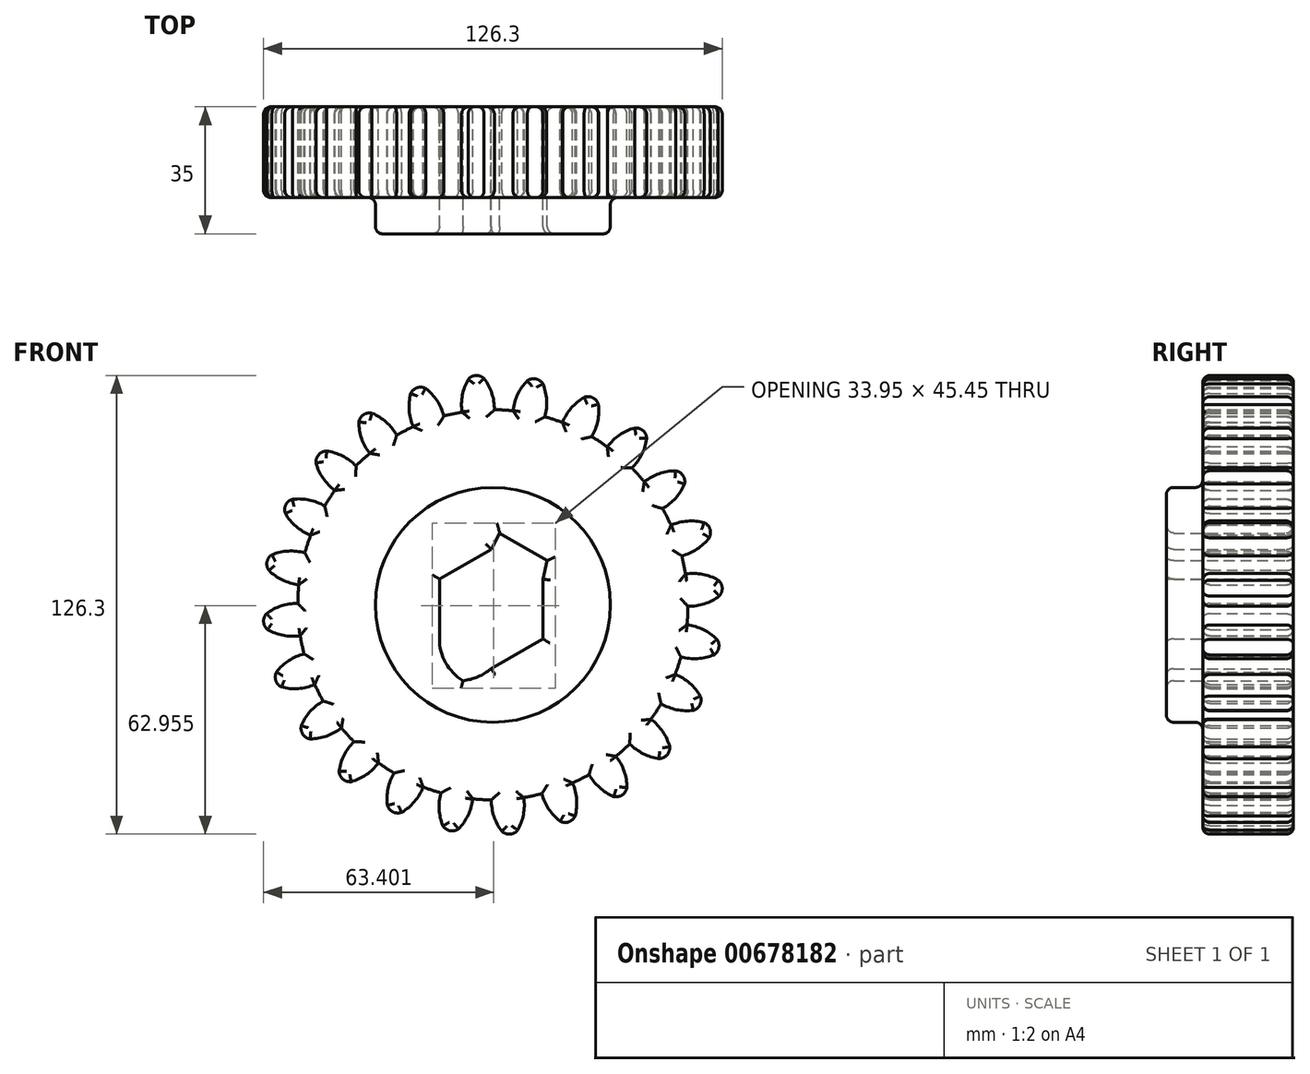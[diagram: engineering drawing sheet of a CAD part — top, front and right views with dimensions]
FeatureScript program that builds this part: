
annotation { "Feature Type Name" : "Feature", "Feature Type Description" : "" }
export const myFeature = defineFeature(function(context is Context, id is Id, definition is map)
    precondition{}
    {
        {
            var Q0;
            Q0=qCreatedBy(makeId("Front.planeOp"),FACE);
            var sketch = newSketch(context, id + "F0", { "sketchPlane" : qUnion([Q0])});
            skCircle(sketch, "E0", {"center": v(0, 0) * mm, "radius": 53.72 * mm});
            skCircle(sketch, "E1", {"center": v(0, 0) * mm, "radius": 58.67 * mm, "construction": true});
            skCircle(sketch, "E2", {"center": v(-0.47, -1.14) * mm, "radius": 63.5 * mm, "construction": true});
            skLineSegment(sketch, "E3", {"start": v(-0.47, -1.14) * mm, "end": v(-0.47, 99.1) * mm, "construction": true});
            skLineSegment(sketch, "E4", {"start": v(-0.47, -1.14) * mm, "end": v(-8.55, 122.05) * mm, "construction": true});
            skLineSegment(sketch, "E5", {"start": v(-0.47, 58.67) * mm, "end": v(-120.67, 58.67) * mm, "construction": true});
            skLineSegment(sketch, "E6", {"start": v(-0.47, 58.67) * mm, "end": v(-118.08, 15.87) * mm, "construction": true});
            skCircle(sketch, "E7", {"center": v(-0.47, -1.14) * mm, "radius": 56.2 * mm, "construction": true});
            skCircle(sketch, "E8", {"center": v(-0.47, 58.67) * mm, "radius": 14.6 * mm, "construction": true});
            skCircle(sketch, "E9", {"center": v(-14.2, 53.68) * mm, "radius": 14.6 * mm, "construction": true});
            skArc(sketch, "E10", {"start": v(0.4, 53.72) * mm, "mid": v(-0.3, 58.26) * mm, "end": v(-2.43, 62.33) * mm});
            skArc(sketch, "E11.MirrorCS", {"start": v(-8.5, 53.14) * mm, "mid": v(-8.4, 57.73) * mm, "end": v(-6.81, 62.05) * mm});
            skLineSegment(sketch, "E12", {"start": v(-8.5, 53.14) * mm, "end": v(-8.5, 53.04) * mm});
            skLineSegment(sketch, "E13", {"start": v(-8.5, 53.04) * mm, "end": v(-8.5, 53.04) * mm});
            skArc(sketch, "E14", {"start": v(-2.43, 62.33) * mm, "mid": v(-4.68, 63.15) * mm, "end": v(-6.81, 62.05) * mm});
            skCircle(sketch, "E15", {"center": v(0, 0) * mm, "radius": 32.33 * mm});
            skCircle(sketch, "E16.cCircle", {"center": v(-0.47, -1.14) * mm, "radius": 14.24 * mm, "construction": true});
            skLineSegment(sketch, "E16.0", {"start": v(13.75, -9.38) * mm, "end": v(-0.5, -17.57) * mm});
            skLineSegment(sketch, "E16.1", {"start": v(-0.5, -17.57) * mm, "end": v(-14.72, -9.33) * mm});
            skLineSegment(sketch, "E16.2", {"start": v(-14.72, -9.33) * mm, "end": v(-14.7, 7.11) * mm});
            skLineSegment(sketch, "E16.3", {"start": v(-14.7, 7.11) * mm, "end": v(-0.44, 15.3) * mm});
            skLineSegment(sketch, "E16.4", {"start": v(-0.44, 15.3) * mm, "end": v(13.78, 7.06) * mm});
            skLineSegment(sketch, "E16.5", {"start": v(13.78, 7.06) * mm, "end": v(13.75, -9.38) * mm});
            skPoint(sketch, "E16.0.midPoint", {"position": v(6.62, -13.48) * mm});
            skLineSegment(sketch, "E17", {"start": v(-0.44, 15.3) * mm, "end": v(1.91, 19.76) * mm});
            skLineSegment(sketch, "E18", {"start": v(1.91, 19.76) * mm, "end": v(14.95, 12.2) * mm});
            skLineSegment(sketch, "E19", {"start": v(14.95, 12.2) * mm, "end": v(13.78, 7.06) * mm});
            skArc(sketch, "E20", {"start": v(-8.23, -20.88) * mm, "mid": v(-4.12, -19.81) * mm, "end": v(-0.5, -17.57) * mm});
            skArc(sketch, "E21", {"start": v(-14.72, -9.33) * mm, "mid": v(-13, -15.95) * mm, "end": v(-8.23, -20.88) * mm});
            skSolve(sketch);
        }
        {
            var Q0;
            {var subQ1=sQuery(id+"F0.wireOp",EDGE,"E10");Q0=makeQuery(id+"F0.imprint","IMPRINT",FACE,{"disambiguationData":[TD([[makeQuery(id+"F0.imprint","IMPRINT",EDGE,{"derivedFrom":subQ1}),1.0]])]});}
            var Q1;
            {var subQ0=sQuery(id+"F0.wireOp",EDGE,"E0");var subQ1=makeQuery(id+"F0.imprint","INTERSECT",VERTEX,{"derivedFrom":[subQ0,sQuery(id+"F0.wireOp",EDGE,"E10")]});Q1=makeQuery(id+"F0.imprint","IMPRINT",FACE,{"disambiguationData":[TD([[makeQuery(id+"F0.imprint","IMPRINT",EDGE,{"disambiguationData":[TD([[subQ1,-1.0]])],"derivedFrom":subQ0}),1.0]])]});}
            extrude(context, id + "F1", {"entities" : qUnion([Q0, Q1]), "depth" : 25 * mm, "offsetDistance" : 25 * mm});
        }
        {
            var Q0;
            Q0=makeQuery(id+"F1.opExtrude","SWEPT_BODY",BODY,{"disambiguationData":[OSD([sQuery(id+"F0.wireOp",EDGE,"E0"),sQuery(id+"F0.wireOp",EDGE,"E10"),sQuery(id+"F0.wireOp",EDGE,"E11.MirrorCS"),sQuery(id+"F0.wireOp",EDGE,"E12"),sQuery(id+"F0.wireOp",EDGE,"E14")])]});
            var Q1;
            Q1=makeQuery(id+"F1.opExtrude","SWEPT_FACE",FACE,{"disambiguationData":[OSD([sQuery(id+"F0.wireOp",EDGE,"E0")])]});
            circularPattern(context, id + "F2", {"entities" : qUnion([Q0]), "axis" : qUnion([Q1]), "angle" : 360 * degree, "instanceCount" : 24, "equalSpace" : true});
        }
        {
            var Q0;
            Q0=makeQuery(id+"F0.imprint","IMPRINT",FACE,{"disambiguationData":[TD([[makeQuery(id+"F0.imprint","IMPRINT",EDGE,{"derivedFrom":sQuery(id+"F0.wireOp",EDGE,"E15")}),1.0]])]});
            extrude(context, id + "F3", {"entities" : qUnion([Q0]), "operationType" : NewBodyOperationType.ADD, "depth" : 35 * mm, "offsetDistance" : 25 * mm});
        }
        {
            var Q0;
            {var subQ0=makeQuery(id+"F1.opExtrude","CAP_FACE",FACE,{"disambiguationData":[OSD([sQuery(id+"F0.wireOp",EDGE,"E0"),sQuery(id+"F0.wireOp",EDGE,"E10"),sQuery(id+"F0.wireOp",EDGE,"E11.MirrorCS"),sQuery(id+"F0.wireOp",EDGE,"E12"),sQuery(id+"F0.wireOp",EDGE,"E14"),sQuery(id+"F0.wireOp",EDGE,"E15")])],"isStart":false});Q0=makeQuery(id+"F3.boolean.opBoolean","MERGE",FACE,{"derivedFrom":[subQ0,makeQuery(id+"F2.opPattern","COPY",FACE,{"derivedFrom":subQ0,"instanceName":"1"}),makeQuery(id+"F2.opPattern","COPY",FACE,{"derivedFrom":subQ0,"instanceName":"2"}),makeQuery(id+"F2.opPattern","COPY",FACE,{"derivedFrom":subQ0,"instanceName":"3"}),makeQuery(id+"F2.opPattern","COPY",FACE,{"derivedFrom":subQ0,"instanceName":"4"}),makeQuery(id+"F2.opPattern","COPY",FACE,{"derivedFrom":subQ0,"instanceName":"5"}),makeQuery(id+"F2.opPattern","COPY",FACE,{"derivedFrom":subQ0,"instanceName":"6"}),makeQuery(id+"F2.opPattern","COPY",FACE,{"derivedFrom":subQ0,"instanceName":"7"}),makeQuery(id+"F2.opPattern","COPY",FACE,{"derivedFrom":subQ0,"instanceName":"8"}),makeQuery(id+"F2.opPattern","COPY",FACE,{"derivedFrom":subQ0,"instanceName":"9"}),makeQuery(id+"F2.opPattern","COPY",FACE,{"derivedFrom":subQ0,"instanceName":"10"}),makeQuery(id+"F2.opPattern","COPY",FACE,{"derivedFrom":subQ0,"instanceName":"11"}),makeQuery(id+"F2.opPattern","COPY",FACE,{"derivedFrom":subQ0,"instanceName":"12"}),makeQuery(id+"F2.opPattern","COPY",FACE,{"derivedFrom":subQ0,"instanceName":"13"}),makeQuery(id+"F2.opPattern","COPY",FACE,{"derivedFrom":subQ0,"instanceName":"14"}),makeQuery(id+"F2.opPattern","COPY",FACE,{"derivedFrom":subQ0,"instanceName":"15"}),makeQuery(id+"F2.opPattern","COPY",FACE,{"derivedFrom":subQ0,"instanceName":"16"}),makeQuery(id+"F2.opPattern","COPY",FACE,{"derivedFrom":subQ0,"instanceName":"17"}),makeQuery(id+"F2.opPattern","COPY",FACE,{"derivedFrom":subQ0,"instanceName":"18"}),makeQuery(id+"F2.opPattern","COPY",FACE,{"derivedFrom":subQ0,"instanceName":"19"}),makeQuery(id+"F2.opPattern","COPY",FACE,{"derivedFrom":subQ0,"instanceName":"20"}),makeQuery(id+"F2.opPattern","COPY",FACE,{"derivedFrom":subQ0,"instanceName":"21"}),makeQuery(id+"F2.opPattern","COPY",FACE,{"derivedFrom":subQ0,"instanceName":"22"}),makeQuery(id+"F2.opPattern","COPY",FACE,{"derivedFrom":subQ0,"instanceName":"23"})]});}
            var Q1;
            {var subQ0=sQuery(id+"F0.wireOp",EDGE,"E15");var subQ1=makeQuery(id+"F1.opExtrude","CAP_FACE",FACE,{"disambiguationData":[OSD([sQuery(id+"F0.wireOp",EDGE,"E0"),sQuery(id+"F0.wireOp",EDGE,"E10"),sQuery(id+"F0.wireOp",EDGE,"E11.MirrorCS"),sQuery(id+"F0.wireOp",EDGE,"E12"),sQuery(id+"F0.wireOp",EDGE,"E14"),subQ0])],"isStart":true});Q1=makeQuery(id+"F3.boolean.opBoolean","MERGE",FACE,{"derivedFrom":[subQ1,makeQuery(id+"F2.opPattern","COPY",FACE,{"derivedFrom":subQ1,"instanceName":"1"}),makeQuery(id+"F2.opPattern","COPY",FACE,{"derivedFrom":subQ1,"instanceName":"2"}),makeQuery(id+"F2.opPattern","COPY",FACE,{"derivedFrom":subQ1,"instanceName":"3"}),makeQuery(id+"F2.opPattern","COPY",FACE,{"derivedFrom":subQ1,"instanceName":"4"}),makeQuery(id+"F2.opPattern","COPY",FACE,{"derivedFrom":subQ1,"instanceName":"5"}),makeQuery(id+"F2.opPattern","COPY",FACE,{"derivedFrom":subQ1,"instanceName":"6"}),makeQuery(id+"F2.opPattern","COPY",FACE,{"derivedFrom":subQ1,"instanceName":"7"}),makeQuery(id+"F2.opPattern","COPY",FACE,{"derivedFrom":subQ1,"instanceName":"8"}),makeQuery(id+"F2.opPattern","COPY",FACE,{"derivedFrom":subQ1,"instanceName":"9"}),makeQuery(id+"F2.opPattern","COPY",FACE,{"derivedFrom":subQ1,"instanceName":"10"}),makeQuery(id+"F2.opPattern","COPY",FACE,{"derivedFrom":subQ1,"instanceName":"11"}),makeQuery(id+"F2.opPattern","COPY",FACE,{"derivedFrom":subQ1,"instanceName":"12"}),makeQuery(id+"F2.opPattern","COPY",FACE,{"derivedFrom":subQ1,"instanceName":"13"}),makeQuery(id+"F2.opPattern","COPY",FACE,{"derivedFrom":subQ1,"instanceName":"14"}),makeQuery(id+"F2.opPattern","COPY",FACE,{"derivedFrom":subQ1,"instanceName":"15"}),makeQuery(id+"F2.opPattern","COPY",FACE,{"derivedFrom":subQ1,"instanceName":"16"}),makeQuery(id+"F2.opPattern","COPY",FACE,{"derivedFrom":subQ1,"instanceName":"17"}),makeQuery(id+"F2.opPattern","COPY",FACE,{"derivedFrom":subQ1,"instanceName":"18"}),makeQuery(id+"F2.opPattern","COPY",FACE,{"derivedFrom":subQ1,"instanceName":"19"}),makeQuery(id+"F2.opPattern","COPY",FACE,{"derivedFrom":subQ1,"instanceName":"20"}),makeQuery(id+"F2.opPattern","COPY",FACE,{"derivedFrom":subQ1,"instanceName":"21"}),makeQuery(id+"F2.opPattern","COPY",FACE,{"derivedFrom":subQ1,"instanceName":"22"}),makeQuery(id+"F2.opPattern","COPY",FACE,{"derivedFrom":subQ1,"instanceName":"23"}),makeQuery(id+"F3.opExtrude","CAP_FACE",FACE,{"disambiguationData":[OSD([subQ0,sQuery(id+"F0.wireOp",EDGE,"E16.0"),sQuery(id+"F0.wireOp",EDGE,"E16.2"),sQuery(id+"F0.wireOp",EDGE,"E16.3"),sQuery(id+"F0.wireOp",EDGE,"E16.5"),sQuery(id+"F0.wireOp",EDGE,"E17"),sQuery(id+"F0.wireOp",EDGE,"E18"),sQuery(id+"F0.wireOp",EDGE,"E19"),sQuery(id+"F0.wireOp",EDGE,"E20"),sQuery(id+"F0.wireOp",EDGE,"E21")])],"isStart":true})]});}
            var Q2;
            Q2=makeQuery(id+"F3.opExtrude","CAP_FACE",FACE,{"disambiguationData":[OSD([sQuery(id+"F0.wireOp",EDGE,"E15"),sQuery(id+"F0.wireOp",EDGE,"E16.0"),sQuery(id+"F0.wireOp",EDGE,"E16.2"),sQuery(id+"F0.wireOp",EDGE,"E16.3"),sQuery(id+"F0.wireOp",EDGE,"E16.5"),sQuery(id+"F0.wireOp",EDGE,"E17"),sQuery(id+"F0.wireOp",EDGE,"E18"),sQuery(id+"F0.wireOp",EDGE,"E19"),sQuery(id+"F0.wireOp",EDGE,"E20"),sQuery(id+"F0.wireOp",EDGE,"E21")])],"isStart":false});
            fillet(context, id + "F4", {"entities" : qUnion([Q0, Q1, Q2]), "radius" : 2 * mm, "tangentPropagation" : true, "allowEdgeOverflow" : false});
        }
    });
